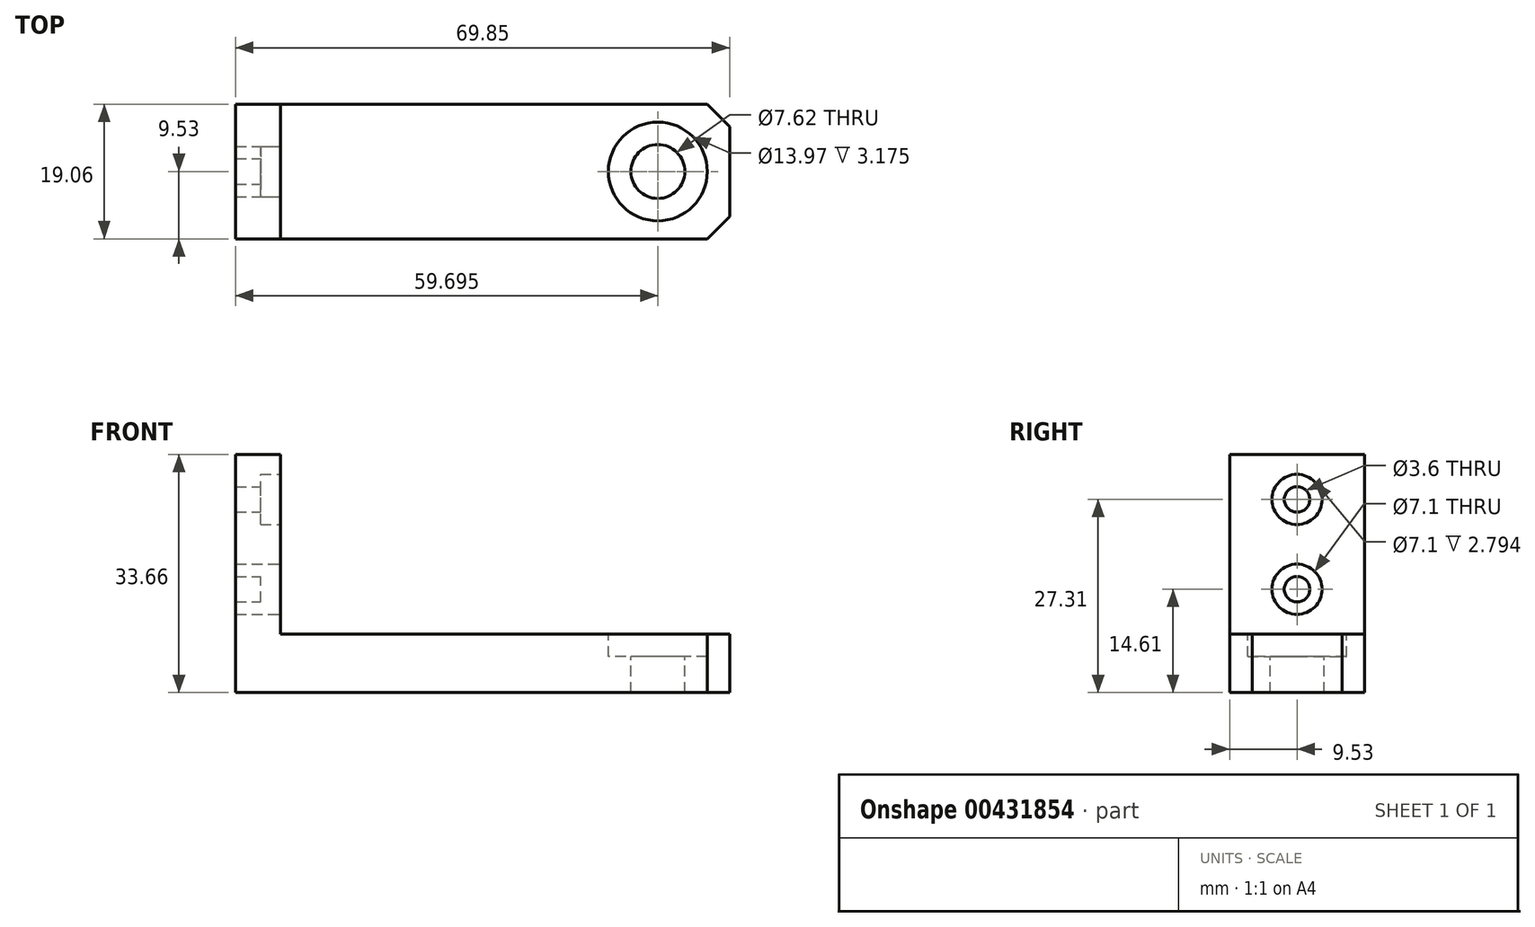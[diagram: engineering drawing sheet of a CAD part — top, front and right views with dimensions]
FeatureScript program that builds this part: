
annotation { "Feature Type Name" : "Feature", "Feature Type Description" : "" }
export const myFeature = defineFeature(function(context is Context, id is Id, definition is map)
    precondition{}
    {
        {
            var Q0;
            Q0=qCreatedBy(makeId("Top.planeOp"),FACE);
            var sketch = newSketch(context, id + "F0", { "sketchPlane" : qUnion([Q0])});
            skLineSegment(sketch, "E0.bottom", {"start": v(34.93, 9.52) * mm, "end": v(-34.93, 9.53) * mm});
            skLineSegment(sketch, "E0.top", {"start": v(34.93, -9.53) * mm, "end": v(-34.93, -9.52) * mm});
            skLineSegment(sketch, "E0.left", {"start": v(34.93, 9.52) * mm, "end": v(34.93, -9.53) * mm});
            skLineSegment(sketch, "E0.right", {"start": v(-34.93, 9.52) * mm, "end": v(-34.93, -9.52) * mm});
            skPoint(sketch, "E0.middle", {"position": v(0, 0) * mm});
            skLineSegment(sketch, "E1", {"start": v(34.93, 0) * mm, "end": v(-34.93, 0) * mm, "construction": true});
            skCircle(sketch, "E2", {"center": v(24.77, 0) * mm, "radius": 3.81 * mm});
            skLineSegment(sketch, "E3.0", {"start": v(-28.58, 9.52) * mm, "end": v(-28.58, -9.53) * mm});
            skCircle(sketch, "E4", {"center": v(24.77, 0) * mm, "radius": 6.99 * mm});
            skSolve(sketch);
        }
        {
            var Q0;
            Q0 = qSketchRegion(id + "F0", true);
            var Q1;
            Q1=makeQuery(id+"F0.imprint","IMPRINT",FACE,{"disambiguationData":[TD([[makeQuery(id+"F0.imprint","IMPRINT",EDGE,{"derivedFrom":sQuery(id+"F0.wireOp",EDGE,"E2")}),-1.0]])]});
            extrude(context, id + "F1", {"entities" : qUnion([Q0, Q1]), "oppositeDirection" : true, "depth" : 8.25 * mm});
        }
        {
            var Q0;
            {var subQ0=sQuery(id+"F0.wireOp",EDGE,"E0.right");Q0=makeQuery(id+"F0.imprint","IMPRINT",FACE,{"disambiguationData":[TD([[makeQuery(id+"F0.imprint","IMPRINT",EDGE,{"derivedFrom":subQ0}),1.0]])]});}
            extrude(context, id + "F2", {"entities" : qUnion([Q0]), "operationType" : NewBodyOperationType.ADD, "depth" : 25.4 * mm});
        }
        {
            var Q0;
            Q0=makeQuery(id+"F0.imprint","IMPRINT",FACE,{"disambiguationData":[TD([[makeQuery(id+"F0.imprint","IMPRINT",EDGE,{"derivedFrom":sQuery(id+"F0.wireOp",EDGE,"E2")}),-1.0]])]});
            extrude(context, id + "F3", {"entities" : qUnion([Q0]), "operationType" : NewBodyOperationType.REMOVE, "oppositeDirection" : true, "depth" : 3.17 * mm});
        }
        {
            var Q0;
            Q0=makeQuery(id+"F2.opExtrude","SWEPT_FACE",FACE,{"disambiguationData":[OSD([sQuery(id+"F0.wireOp",EDGE,"E3.0")])]});
            var sketch = newSketch(context, id + "F4", { "sketchPlane" : qUnion([Q0])});
            skLineSegment(sketch, "E5", {"start": v(0, 25.4) * mm, "end": v(0, 0) * mm, "construction": true});
            skLineSegment(sketch, "E6", {"start": v(9.53, 12.7) * mm, "end": v(-9.53, 12.7) * mm, "construction": true});
            skCircle(sketch, "E7", {"center": v(0, 19.05) * mm, "radius": 1.8 * mm});
            skCircle(sketch, "E8.MirrorC", {"center": v(0, 6.35) * mm, "radius": 1.8 * mm});
            skCircle(sketch, "E9.0", {"center": v(0, 6.35) * mm, "radius": 3.55 * mm});
            skCircle(sketch, "E10.MirrorC", {"center": v(0, 19.05) * mm, "radius": 3.55 * mm});
            skSolve(sketch);
        }
        {
            var Q0;
            Q0=makeQuery(id+"F4.imprint","IMPRINT",FACE,{"disambiguationData":[TD([[makeQuery(id+"F4.imprint","IMPRINT",EDGE,{"derivedFrom":sQuery(id+"F4.wireOp",EDGE,"E8.MirrorC")}),-1.0]])]});
            var Q1;
            Q1=makeQuery(id+"F4.imprint","IMPRINT",FACE,{"disambiguationData":[TD([[makeQuery(id+"F4.imprint","IMPRINT",EDGE,{"derivedFrom":sQuery(id+"F4.wireOp",EDGE,"E7")}),1.0]])]});
            var Q2;
            {var subQ0=sQuery(id+"F0.wireOp",EDGE,"E0.right");Q2=makeQuery(id+"F2.boolean.opBoolean","MERGE",FACE,{"derivedFrom":[makeQuery(id+"F1.opExtrude","SWEPT_FACE",FACE,{"disambiguationData":[OSD([subQ0])]}),makeQuery(id+"F2.opExtrude","SWEPT_FACE",FACE,{"disambiguationData":[OSD([subQ0])]})]});}
            extrude(context, id + "F5", {"entities" : qUnion([Q0, Q1]), "operationType" : NewBodyOperationType.REMOVE, "endBound" : BoundingType.UP_TO_SURFACE, "oppositeDirection" : true, "endBoundEntityFace" : qUnion([Q2]), "depth" : 25.4 * mm});
        }
        {
            var Q0;
            Q0=makeQuery(id+"F2.opExtrude","CAP_EDGE",EDGE,{"disambiguationData":[OSD([sQuery(id+"F0.wireOp",EDGE,"E3.0")])],"isStart":true});
            var Q1;
            Q1=makeQuery(id+"F1.opExtrude","SWEPT_EDGE",EDGE,{"disambiguationData":[OSD([sQuery(id+"F0.wireOp",EDGE,"E0.bottom"),sQuery(id+"F0.wireOp",EDGE,"E0.left")])]});
            var Q2;
            Q2=makeQuery(id+"F1.opExtrude","SWEPT_EDGE",EDGE,{"disambiguationData":[OSD([sQuery(id+"F0.wireOp",EDGE,"E0.top"),sQuery(id+"F0.wireOp",EDGE,"E0.left")])]});
            chamfer(context, id + "F6", {"entities" : qUnion([Q0, Q1, Q2]), "width" : 3.17 * mm, "tangentPropagation" : true});
        }
        {
            var Q0;
            Q0=makeQuery(id+"F4.imprint","IMPRINT",FACE,{"disambiguationData":[TD([[makeQuery(id+"F4.imprint","IMPRINT",EDGE,{"derivedFrom":sQuery(id+"F4.wireOp",EDGE,"E8.MirrorC")}),1.0]])]});
            var Q1;
            Q1=makeQuery(id+"F4.imprint","IMPRINT",FACE,{"disambiguationData":[TD([[makeQuery(id+"F4.imprint","IMPRINT",EDGE,{"derivedFrom":sQuery(id+"F4.wireOp",EDGE,"E7")}),-1.0]])]});
            extrude(context, id + "F7", {"entities" : qUnion([Q0, Q1]), "operationType" : NewBodyOperationType.REMOVE, "oppositeDirection" : true, "depth" : 2.8 * mm});
        }
    });
